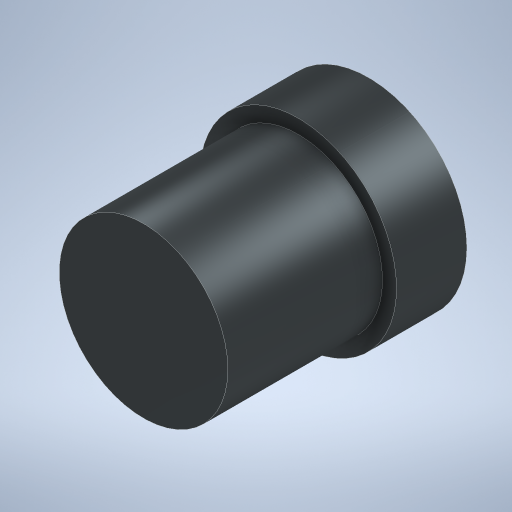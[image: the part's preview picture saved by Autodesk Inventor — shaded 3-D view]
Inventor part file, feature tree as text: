
AUTODESK INVENTOR PART (.ipt)
format: ipt  version: 2023 (Build 270158000, 158)  size: 235,520 bytes
history: native  units: mm
features: extrude x2, sketch x2
ambient origin geometry x8: Origin, YZ Plane, XZ Plane, XY Plane, X Axis, Y Axis, Z Axis, Center Point
bodies: Solid1 (feature_tree)
feature tree (4):
  extrude  "Extrusion1"  Depth=5.0mm TaperAngle=0.0deg
  extrude  "Extrusion2"  Depth=11.0mm TaperAngle=0.0deg
  sketch  "Sketch1"  dims[d0=14.0mm d1=5.0mm d2=0.0mm]
  sketch  "Sketch2"  dims[d3=12.0mm d4=11.0mm d5=0.0mm]
